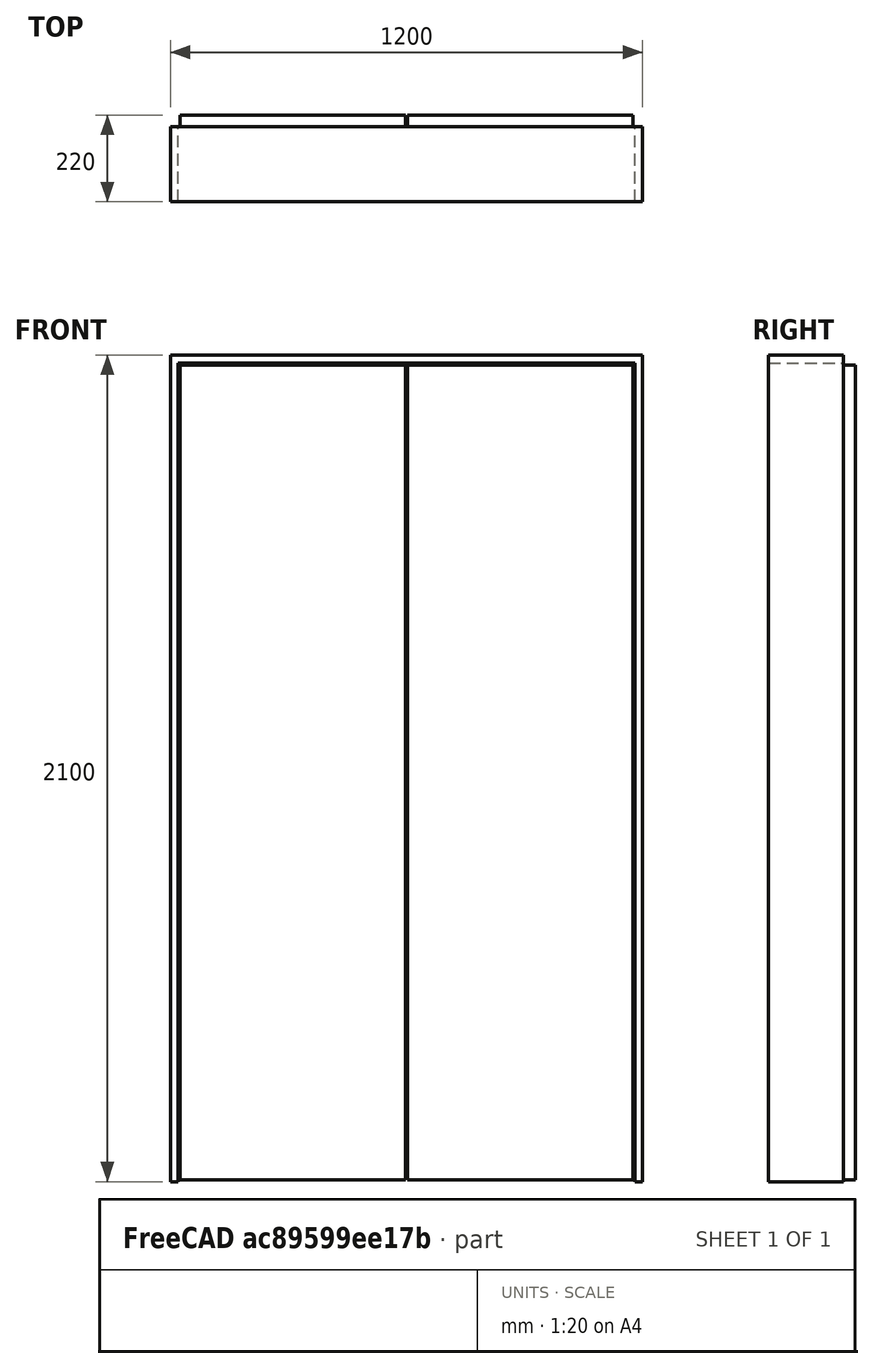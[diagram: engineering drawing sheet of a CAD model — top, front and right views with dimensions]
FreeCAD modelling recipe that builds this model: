
FCSTD DOCUMENT  (FreeCAD 0.16R6704 (Git))
Label: Elevator doors
License: CreativeCommons Attribution
LicenseURL: http://creativecommons.org/licenses/by/4.0/
objects: Sketcher::SketchObject×1, Part::FeaturePython×1
note: 2 computed .brp shape members not serialized (recipe doc carries the construction recipe); baked Part::Feature solids carry a one-line shape summary decoded from their .brp

FEATURE [Sketcher::SketchObject] Sketch057
  Placement = pos=(0,0,0) rot=(1,0,0;1.5708rad)
  sketch-geometry (17):
    g0: LineSegment StartX=0 StartY=2100 StartZ=0 EndX=1200 EndY=2100 EndZ=0
    g1: LineSegment StartX=1200 StartY=2100 StartZ=0 EndX=1200 EndY=0 EndZ=0
    g2: LineSegment StartX=1200 StartY=0 StartZ=0 EndX=0 EndY=0 EndZ=0
    g3: LineSegment StartX=0 StartY=0 StartZ=0 EndX=0 EndY=2100 EndZ=0
    g4: LineSegment StartX=20 StartY=2080 StartZ=0 EndX=1180 EndY=2080 EndZ=0
    g5: LineSegment StartX=1180 StartY=2080 StartZ=0 EndX=1180 EndY=0 EndZ=0
    g6: LineSegment StartX=1180 StartY=0 StartZ=0 EndX=20 EndY=0 EndZ=0
    g7: LineSegment StartX=20 StartY=0 StartZ=0 EndX=20 EndY=2080 EndZ=0
    g8: LineSegment StartX=25 StartY=2075 StartZ=0 EndX=597.5 EndY=2075 EndZ=0
    g9: LineSegment StartX=597.5 StartY=2075 StartZ=0 EndX=597.5 EndY=5 EndZ=0
    g10: LineSegment StartX=597.5 StartY=5 StartZ=0 EndX=25 EndY=5 EndZ=0
    g11: LineSegment StartX=25 StartY=5 StartZ=0 EndX=25 EndY=2075 EndZ=0
    g12: LineSegment StartX=602.5 StartY=2075 StartZ=0 EndX=1175 EndY=2075 EndZ=0
    g13: LineSegment StartX=1175 StartY=2075 StartZ=0 EndX=1175 EndY=5 EndZ=0
    g14: LineSegment StartX=1175 StartY=5 StartZ=0 EndX=602.5 EndY=5 EndZ=0
    g15: LineSegment StartX=602.5 StartY=5 StartZ=0 EndX=602.5 EndY=2075 EndZ=0
    g16: LineSegment [constr] StartX=600 StartY=2271.85 StartZ=0 EndX=600 EndY=-280.023 EndZ=0
  constraints (47):
    c: Coincident(g0,g1)
    c: Coincident(g1,g2)
    c: Horizontal(g0)
    c: Horizontal(g2)
    c: Vertical(g1)
    c: DistanceX(g0,g0) = 1200  'Largura da abertura'
    c: Coincident(g4,g5)
    c: Coincident(g5,g6)
    c: Coincident(g6,g7)
    c: Coincident(g7,g4)
    c: Horizontal(g6)
    c: Vertical(g5)
    c: Vertical(g7)
    c: PointOnObject(g5,g2)
    c: DistanceX(g0,g4) = 20
    c: DistanceX(g4,g0) = 20
    c: DistanceY(g4,g0) = 20
    c: Coincident(g8,g9)
    c: Coincident(g9,g10)
    c: Coincident(g10,g11)
    c: Coincident(g11,g8)
    c: Horizontal(g10)
    c: Vertical(g9)
    c: Vertical(g11)
    c: Coincident(g12,g13)
    c: Coincident(g13,g14)
    c: Coincident(g14,g15)
    c: Coincident(g15,g12)
    c: Horizontal(g14)
    c: Vertical(g13)
    c: Vertical(g15)
    c: DistanceX(g4,g8) = 5
    c: DistanceY(g10,g6) = -5
    c: DistanceX(g12,g4) = 5
    c: DistanceY(g13,g5) = -5
    c: DistanceX(g8,g12) = 5
    c: Symmetric(g8,g12,g16)
    c: Symmetric(g8,g12,g16)
    c: Horizontal(g8)
    c: Horizontal(g12)
    c: Horizontal(g4)
    c: DistanceY(g8,g4) = 5
    c: Coincident(g0,g3)
    c: Coincident(g2,g3)
    c: Vertical(g3)
    c: Coincident(g2,g-1)
    c: DistanceY(g-1,g0) = 2100  'Altura da abertura'
FEATURE [Part::FeaturePython] Window055  label="Elevator doors "  # WARN: FeaturePython — macro-defined, semantics opaque (R4)
  Base = -> Sketch057
  Height = 0
  HoleDepth = 0
  MoveWithHost = true
  Normal = (0,1,0)
  Preset = 0
  Role = 0
  Width = 0
  WindowParts = BATENTE | Frame | Wire0,Wire1 | 190.0 | 0.0 | PORTA 1 | Solid panel | Wire2 | 30.0 | 190.0 | PORTA 2 | Solid panel | Wire3 | 30.0 | 190.0
